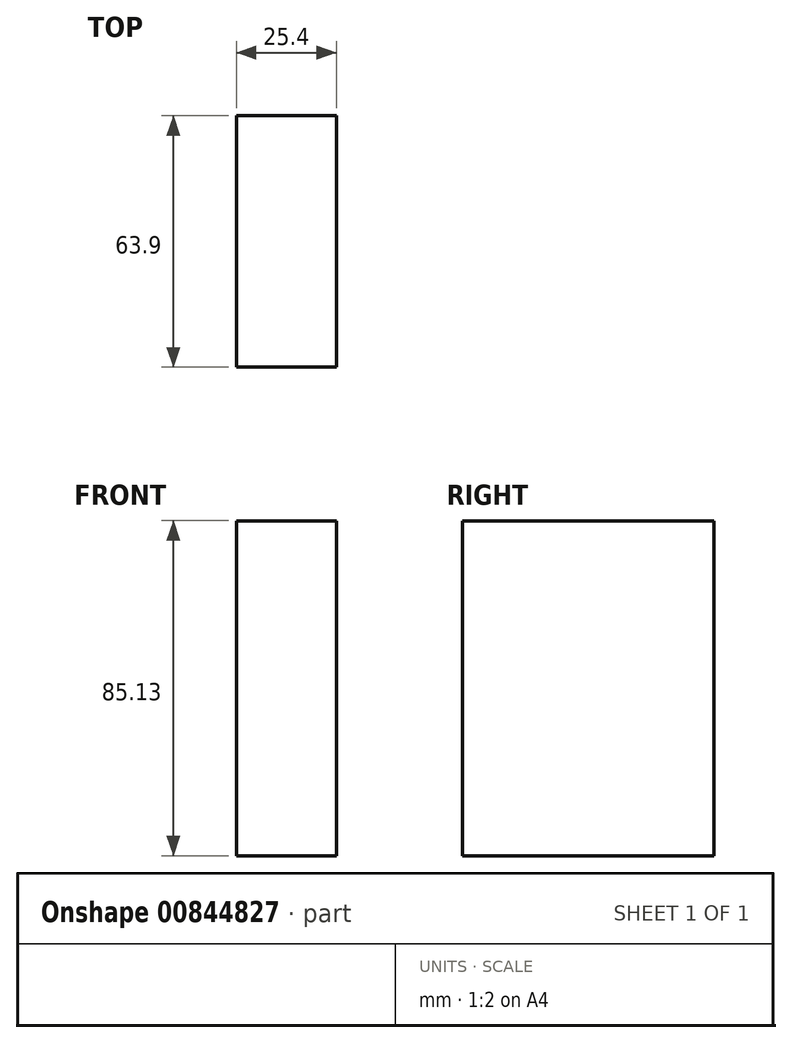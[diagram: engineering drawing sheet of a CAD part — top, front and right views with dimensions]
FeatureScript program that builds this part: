
annotation { "Feature Type Name" : "Feature", "Feature Type Description" : "" }
export const myFeature = defineFeature(function(context is Context, id is Id, definition is map)
    precondition{}
    {
        {
            var Q0;
            Q0=qCreatedBy(makeId("Right.planeOp"),FACE);
            var sketch = newSketch(context, id + "F0", { "sketchPlane" : qUnion([Q0])});
            skLineSegment(sketch, "E0.bottom", {"start": v(-26.97, 59.72) * mm, "end": v(36.93, 59.72) * mm});
            skLineSegment(sketch, "E0.top", {"start": v(-26.97, -25.41) * mm, "end": v(36.93, -25.41) * mm});
            skLineSegment(sketch, "E0.left", {"start": v(-26.97, 59.72) * mm, "end": v(-26.97, -25.41) * mm});
            skLineSegment(sketch, "E0.right", {"start": v(36.93, 59.72) * mm, "end": v(36.93, -25.41) * mm});
            skSolve(sketch);
        }
        {
            var Q0;
            Q0=makeQuery(id+"F0.imprint","IMPRINT",FACE,{"disambiguationData":[TD([[makeQuery(id+"F0.imprint","IMPRINT",EDGE,{"derivedFrom":sQuery(id+"F0.wireOp",EDGE,"E0.bottom")}),-1.0]])]});
            extrude(context, id + "F1", {"entities" : qUnion([Q0]), "depth" : 25.4 * mm, "offsetDistance" : 25.4 * mm});
        }
    });
